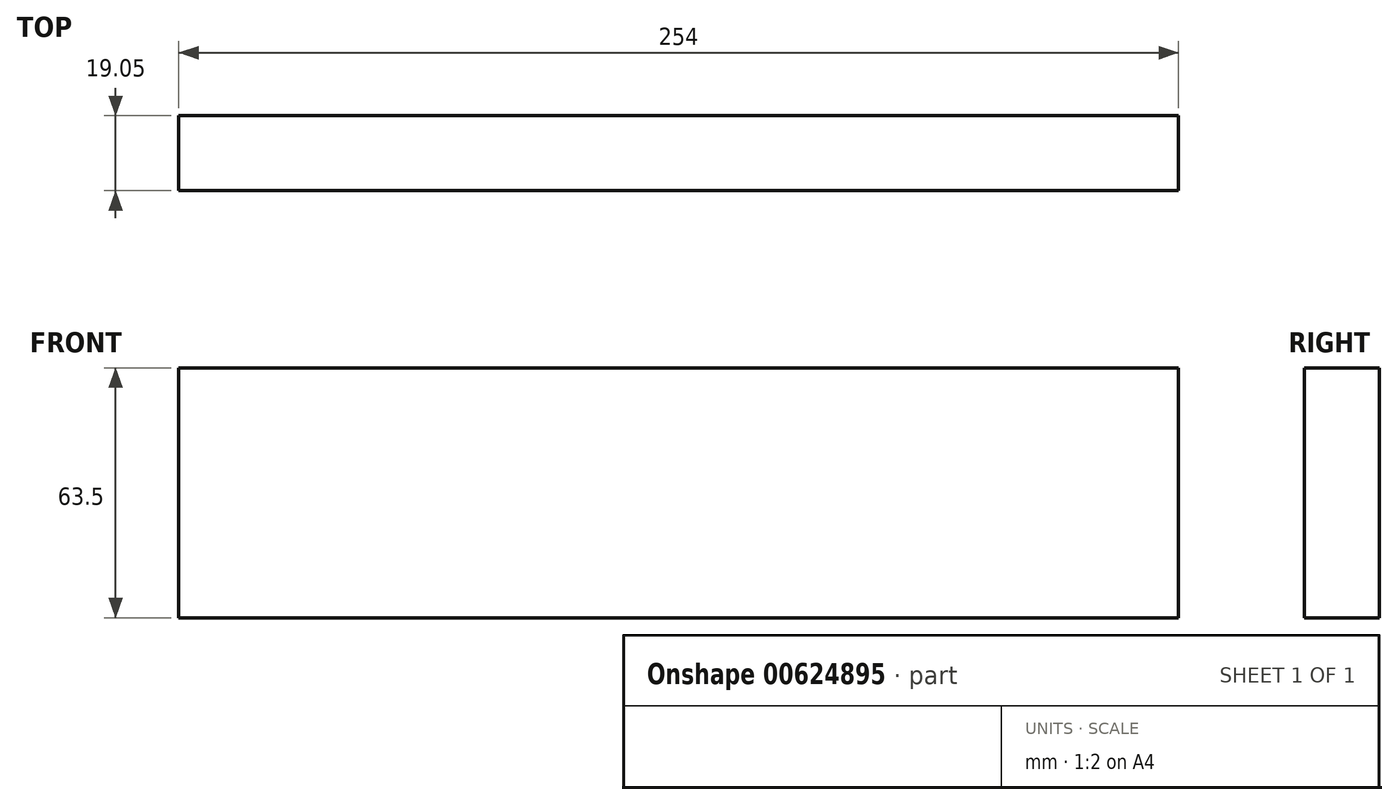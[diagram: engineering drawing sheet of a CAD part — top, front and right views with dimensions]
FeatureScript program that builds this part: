
annotation { "Feature Type Name" : "Feature", "Feature Type Description" : "" }
export const myFeature = defineFeature(function(context is Context, id is Id, definition is map)
    precondition{}
    {
        {
            var Q0;
            Q0=qCreatedBy(makeId("Front.planeOp"),FACE);
            var sketch = newSketch(context, id + "F0", { "sketchPlane" : qUnion([Q0])});
            skLineSegment(sketch, "E0.bottom", {"start": v(0, 0) * mm, "end": v(-254, 0) * mm});
            skLineSegment(sketch, "E0.top", {"start": v(0, 63.5) * mm, "end": v(-254, 63.5) * mm});
            skLineSegment(sketch, "E0.left", {"start": v(0, 0) * mm, "end": v(0, 63.5) * mm});
            skLineSegment(sketch, "E0.right", {"start": v(-254, 0) * mm, "end": v(-254, 63.5) * mm});
            skSolve(sketch);
        }
        {
            var Q0;
            Q0=makeQuery(id+"F0.imprint","IMPRINT",FACE,{"disambiguationData":[TD([[makeQuery(id+"F0.imprint","IMPRINT",EDGE,{"derivedFrom":sQuery(id+"F0.wireOp",EDGE,"E0.bottom")}),-1.0]])]});
            extrude(context, id + "F1", {"entities" : qUnion([Q0]), "oppositeDirection" : true, "depth" : 19.05 * mm, "offsetDistance" : 25.4 * mm});
        }
    });
